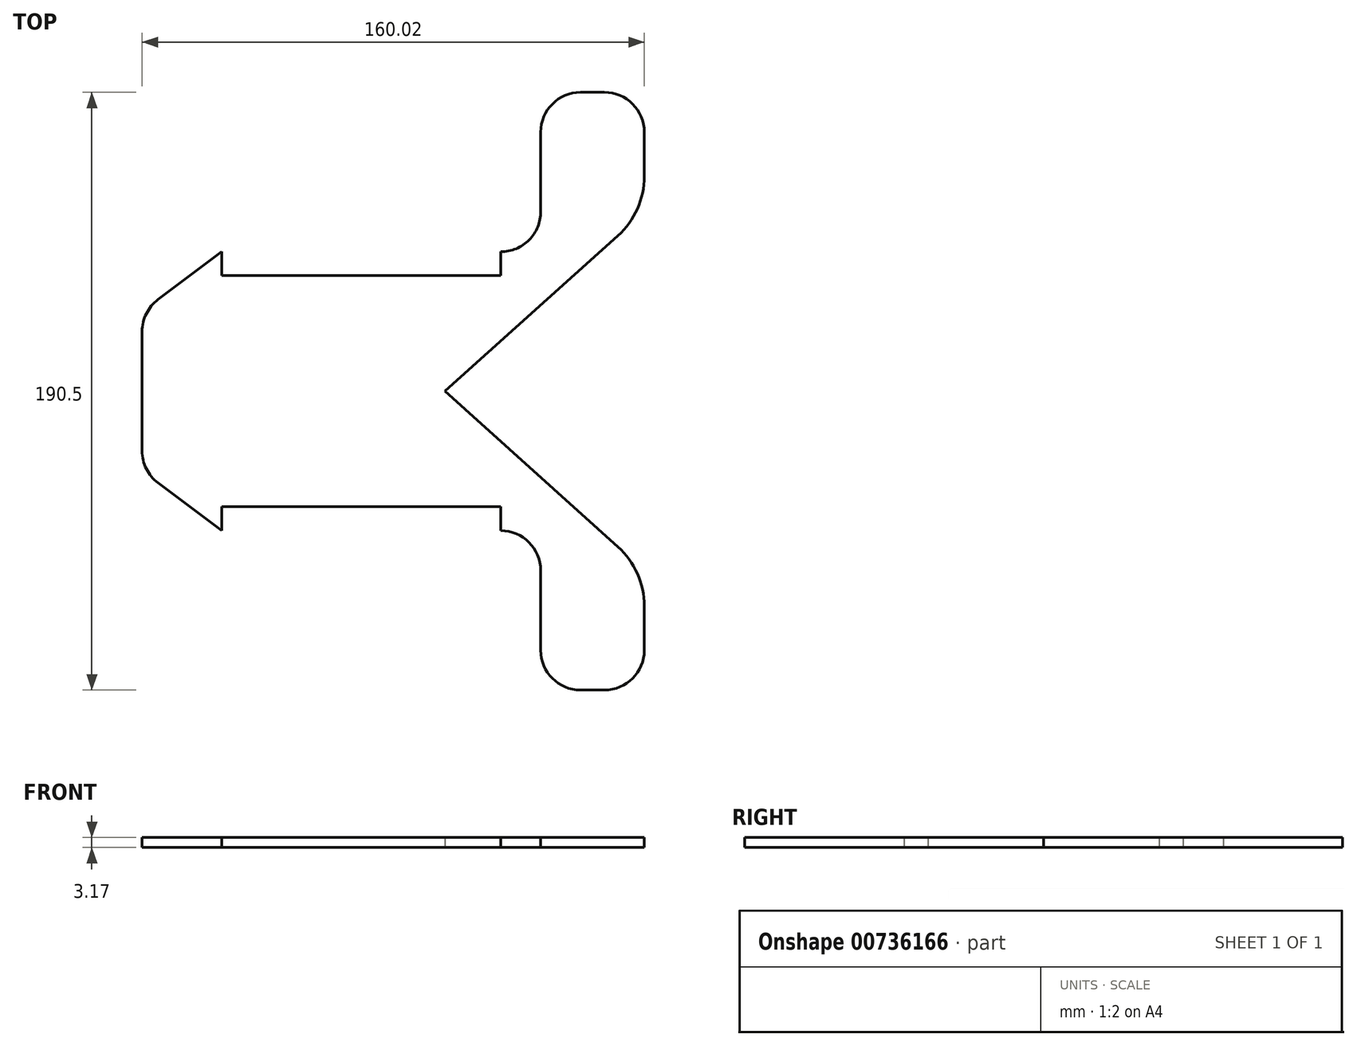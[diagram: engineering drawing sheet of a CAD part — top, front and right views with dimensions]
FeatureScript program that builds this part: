
annotation { "Feature Type Name" : "Feature", "Feature Type Description" : "" }
export const myFeature = defineFeature(function(context is Context, id is Id, definition is map)
    precondition{}
    {
        {
            var Q0;
            Q0=qCreatedBy(makeId("Top.planeOp"),FACE);
            var sketch = newSketch(context, id + "F0", { "sketchPlane" : qUnion([Q0])});
            skArc(sketch, "E0", {"start": v(12.7, -12.7) * mm, "mid": v(8.98, -3.72) * mm, "end": v(0, 0) * mm});
            skLineSegment(sketch, "E1", {"start": v(12.7, 101.6) * mm, "end": v(12.7, 139.7) * mm});
            skLineSegment(sketch, "E2", {"start": v(12.7, -12.7) * mm, "end": v(12.7, -50.8) * mm});
            skLineSegment(sketch, "E3", {"start": v(12.7, -50.8) * mm, "end": v(45.72, -50.8) * mm});
            skLineSegment(sketch, "E4", {"start": v(12.7, 139.7) * mm, "end": v(45.72, 139.7) * mm});
            skLineSegment(sketch, "E5", {"start": v(45.72, 139.7) * mm, "end": v(45.72, 101.6) * mm});
            skLineSegment(sketch, "E6", {"start": v(45.72, -50.8) * mm, "end": v(45.72, -12.7) * mm});
            skLineSegment(sketch, "E7", {"start": v(45.72, -12.7) * mm, "end": v(-17.78, 44.45) * mm});
            skLineSegment(sketch, "E8", {"start": v(-17.78, 44.45) * mm, "end": v(45.72, 101.6) * mm});
            skArc(sketch, "E9", {"start": v(0, 88.9) * mm, "mid": v(9.04, 92.68) * mm, "end": v(12.7, 101.76) * mm});
            skPoint(sketch, "E10", {"position": v(8.98, -3.72) * mm});
            skLineSegment(sketch, "E11", {"start": v(8.98, -3.72) * mm, "end": v(20.96, 9.59) * mm});
            skPoint(sketch, "E12", {"position": v(9.04, 92.68) * mm});
            skLineSegment(sketch, "E13", {"start": v(9.04, 92.68) * mm, "end": v(21.01, 79.37) * mm});
            skLineSegment(sketch, "E14", {"start": v(-88.9, 88.9) * mm, "end": v(-88.9, 81.28) * mm});
            skLineSegment(sketch, "E15", {"start": v(-88.9, 88.9) * mm, "end": v(-114.3, 69.85) * mm});
            skLineSegment(sketch, "E16", {"start": v(-114.3, 69.85) * mm, "end": v(-114.3, 19.05) * mm});
            skLineSegment(sketch, "E17", {"start": v(-114.3, 19.05) * mm, "end": v(-88.9, 0) * mm});
            skLineSegment(sketch, "E18", {"start": v(-78.74, 81.28) * mm, "end": v(-78.74, 68.58) * mm});
            skLineSegment(sketch, "E19", {"start": v(-78.74, 68.58) * mm, "end": v(-78.74, 7.62) * mm});
            skLineSegment(sketch, "E20", {"start": v(-88.9, 81.28) * mm, "end": v(0, 81.28) * mm});
            skLineSegment(sketch, "E21", {"start": v(0, 81.28) * mm, "end": v(0, 88.9) * mm});
            skLineSegment(sketch, "E22", {"start": v(-88.9, 7.62) * mm, "end": v(0, 7.62) * mm});
            skLineSegment(sketch, "E23", {"start": v(0, 7.62) * mm, "end": v(0, 0) * mm});
            skLineSegment(sketch, "E24.trimOffspring", {"start": v(-88.9, 7.62) * mm, "end": v(-88.9, 0) * mm});
            skPoint(sketch, "E25.orphan", {"position": v(-78.74, 88.9) * mm});
            skSolve(sketch);
        }
        {
            var Q0;
            {var subQ3=sQuery(id+"F0.wireOp",EDGE,"E4");Q0=makeQuery(id+"F0.imprint","IMPRINT",FACE,{"disambiguationData":[TD([[makeQuery(id+"F0.imprint","IMPRINT",EDGE,{"derivedFrom":subQ3}),-1.0]])]});}
            var Q1;
            {var subQ5=sQuery(id+"F0.wireOp",EDGE,"E11");Q1=makeQuery(id+"F0.imprint","IMPRINT",FACE,{"disambiguationData":[TD([[makeQuery(id+"F0.imprint","IMPRINT",EDGE,{"derivedFrom":subQ5}),1.0]])]});}
            var Q2;
            {var subQ1=sQuery(id+"F0.wireOp",EDGE,"E2");Q2=makeQuery(id+"F0.imprint","IMPRINT",FACE,{"disambiguationData":[TD([[makeQuery(id+"F0.imprint","IMPRINT",EDGE,{"derivedFrom":subQ1}),1.0]])]});}
            var Q3;
            Q3=makeQuery(id+"F0.imprint","IMPRINT",FACE,{"disambiguationData":[TD([[makeQuery(id+"F0.imprint","IMPRINT",EDGE,{"derivedFrom":sQuery(id+"F0.wireOp",EDGE,"E14")}),-1.0]])]});
            var Q4;
            {var subQ0=sQuery(id+"F0.wireOp",EDGE,"E14");Q4=makeQuery(id+"F0.imprint","IMPRINT",FACE,{"disambiguationData":[TD([[makeQuery(id+"F0.imprint","IMPRINT",EDGE,{"derivedFrom":subQ0}),1.0]])]});}
            extrude(context, id + "F1", {"entities" : qUnion([Q0, Q1, Q2, Q3, Q4]), "depth" : 3.17 * mm, "offsetDistance" : 25.4 * mm});
        }
        {
            var Q0;
            Q0=makeQuery(id+"F1.opExtrude","SWEPT_EDGE",EDGE,{"disambiguationData":[OSD([sQuery(id+"F0.wireOp",EDGE,"E15"),sQuery(id+"F0.wireOp",EDGE,"E16")])]});
            var Q1;
            Q1=makeQuery(id+"F1.opExtrude","SWEPT_EDGE",EDGE,{"disambiguationData":[OSD([sQuery(id+"F0.wireOp",EDGE,"E16"),sQuery(id+"F0.wireOp",EDGE,"E17")])]});
            var Q2;
            Q2=makeQuery(id+"F1.opExtrude","SWEPT_EDGE",EDGE,{"disambiguationData":[OSD([sQuery(id+"F0.wireOp",EDGE,"E2"),sQuery(id+"F0.wireOp",EDGE,"E3")])]});
            var Q3;
            Q3=makeQuery(id+"F1.opExtrude","SWEPT_EDGE",EDGE,{"disambiguationData":[OSD([sQuery(id+"F0.wireOp",EDGE,"E3"),sQuery(id+"F0.wireOp",EDGE,"E6")])]});
            var Q4;
            Q4=makeQuery(id+"F1.opExtrude","SWEPT_EDGE",EDGE,{"disambiguationData":[OSD([sQuery(id+"F0.wireOp",EDGE,"E4"),sQuery(id+"F0.wireOp",EDGE,"E5")])]});
            var Q5;
            Q5=makeQuery(id+"F1.opExtrude","SWEPT_EDGE",EDGE,{"disambiguationData":[OSD([sQuery(id+"F0.wireOp",EDGE,"E1"),sQuery(id+"F0.wireOp",EDGE,"E4")])]});
            fillet(context, id + "F2", {"entities" : qUnion([Q0, Q1, Q2, Q3, Q4, Q5]), "radius" : 12.7 * mm, "tangentPropagation" : true, "allowEdgeOverflow" : false});
        }
        {
            var Q0;
            Q0=makeQuery(id+"F1.opExtrude","SWEPT_EDGE",EDGE,{"disambiguationData":[OSD([sQuery(id+"F0.wireOp",EDGE,"E5"),sQuery(id+"F0.wireOp",EDGE,"E8")])]});
            var Q1;
            Q1=makeQuery(id+"F1.opExtrude","SWEPT_EDGE",EDGE,{"disambiguationData":[OSD([sQuery(id+"F0.wireOp",EDGE,"E6"),sQuery(id+"F0.wireOp",EDGE,"E7")])]});
            fillet(context, id + "F3", {"entities" : qUnion([Q0, Q1]), "radius" : 25.4 * mm, "tangentPropagation" : true, "allowEdgeOverflow" : false});
        }
    });
